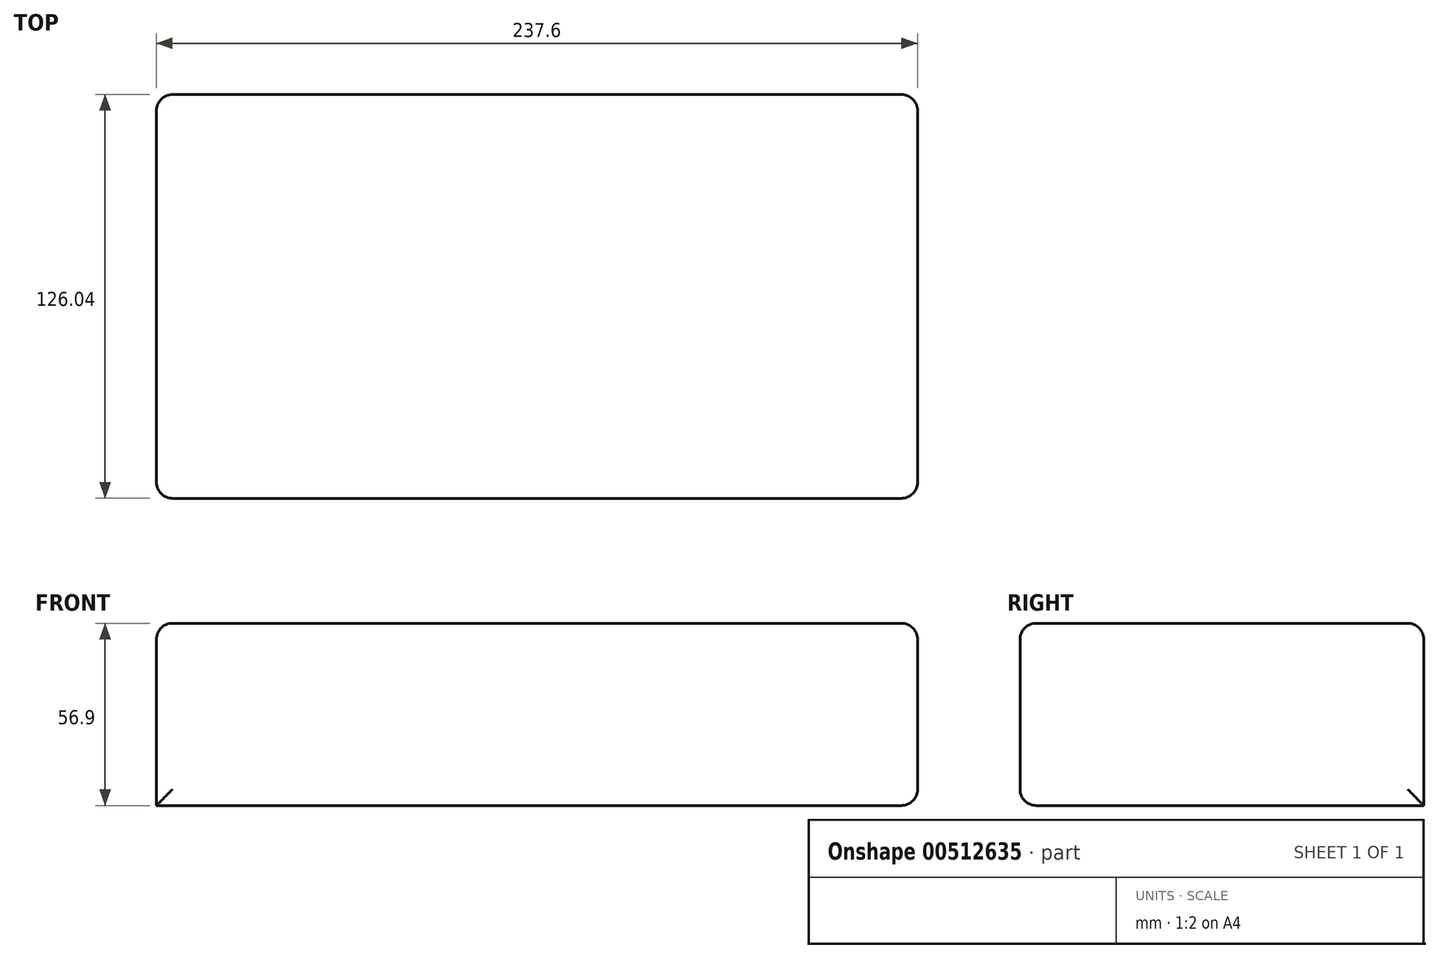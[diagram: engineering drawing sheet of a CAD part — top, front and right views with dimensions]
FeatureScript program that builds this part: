
annotation { "Feature Type Name" : "Feature", "Feature Type Description" : "" }
export const myFeature = defineFeature(function(context is Context, id is Id, definition is map)
    precondition{}
    {
        {
            var Q0;
            Q0=qCreatedBy(makeId("Top.planeOp"),FACE);
            var sketch = newSketch(context, id + "F0", { "sketchPlane" : qUnion([Q0])});
            skLineSegment(sketch, "E0.bottom", {"start": v(-126.58, 68.75) * mm, "end": v(111.02, 68.75) * mm});
            skLineSegment(sketch, "E0.top", {"start": v(-126.58, -57.3) * mm, "end": v(111.02, -57.3) * mm});
            skLineSegment(sketch, "E0.left", {"start": v(-126.58, 68.75) * mm, "end": v(-126.58, -57.3) * mm});
            skLineSegment(sketch, "E0.right", {"start": v(111.02, 68.75) * mm, "end": v(111.02, -57.3) * mm});
            skSolve(sketch);
        }
        {
            var Q0;
            Q0 = qSketchRegion(id + "F0", true);
            extrude(context, id + "F1", {"entities" : qUnion([Q0]), "depth" : 56.9 * mm});
        }
        {
            var Q0;
            Q0=makeQuery(id+"F1.opExtrude","CAP_EDGE",EDGE,{"disambiguationData":[OSD([sQuery(id+"F0.wireOp",EDGE,"E0.top")])],"isStart":false});
            var Q1;
            Q1=makeQuery(id+"F1.opExtrude","CAP_EDGE",EDGE,{"disambiguationData":[OSD([sQuery(id+"F0.wireOp",EDGE,"E0.left")])],"isStart":false});
            var Q2;
            Q2=makeQuery(id+"F1.opExtrude","CAP_EDGE",EDGE,{"disambiguationData":[OSD([sQuery(id+"F0.wireOp",EDGE,"E0.bottom")])],"isStart":false});
            var Q3;
            Q3=makeQuery(id+"F1.opExtrude","CAP_EDGE",EDGE,{"disambiguationData":[OSD([sQuery(id+"F0.wireOp",EDGE,"E0.right")])],"isStart":false});
            var Q4;
            Q4=makeQuery(id+"F1.opExtrude","SWEPT_EDGE",EDGE,{"disambiguationData":[OSD([sQuery(id+"F0.wireOp",EDGE,"E0.bottom"),sQuery(id+"F0.wireOp",EDGE,"E0.right")])]});
            var Q5;
            Q5=makeQuery(id+"F1.opExtrude","SWEPT_EDGE",EDGE,{"disambiguationData":[OSD([sQuery(id+"F0.wireOp",EDGE,"E0.top"),sQuery(id+"F0.wireOp",EDGE,"E0.right")])]});
            var Q6;
            Q6=makeQuery(id+"F1.opExtrude","CAP_EDGE",EDGE,{"disambiguationData":[OSD([sQuery(id+"F0.wireOp",EDGE,"E0.right")])],"isStart":true});
            var Q7;
            Q7=makeQuery(id+"F1.opExtrude","CAP_EDGE",EDGE,{"disambiguationData":[OSD([sQuery(id+"F0.wireOp",EDGE,"E0.top")])],"isStart":true});
            var Q8;
            Q8=makeQuery(id+"F1.opExtrude","SWEPT_EDGE",EDGE,{"disambiguationData":[OSD([sQuery(id+"F0.wireOp",EDGE,"E0.top"),sQuery(id+"F0.wireOp",EDGE,"E0.left")])]});
            fillet(context, id + "F2", {"entities" : qUnion([Q0, Q1, Q2, Q3, Q4, Q5, Q6, Q7, Q8]), "radius" : 5.08 * mm, "tangentPropagation" : true, "allowEdgeOverflow" : false});
        }
        {
            var Q0;
            Q0=makeQuery(id+"F1.opExtrude","SWEPT_EDGE",EDGE,{"disambiguationData":[OSD([sQuery(id+"F0.wireOp",EDGE,"E0.bottom"),sQuery(id+"F0.wireOp",EDGE,"E0.left")])]});
            fillet(context, id + "F3", {"entities" : qUnion([Q0]), "radius" : 5.08 * mm, "tangentPropagation" : true, "allowEdgeOverflow" : false});
        }
    });
